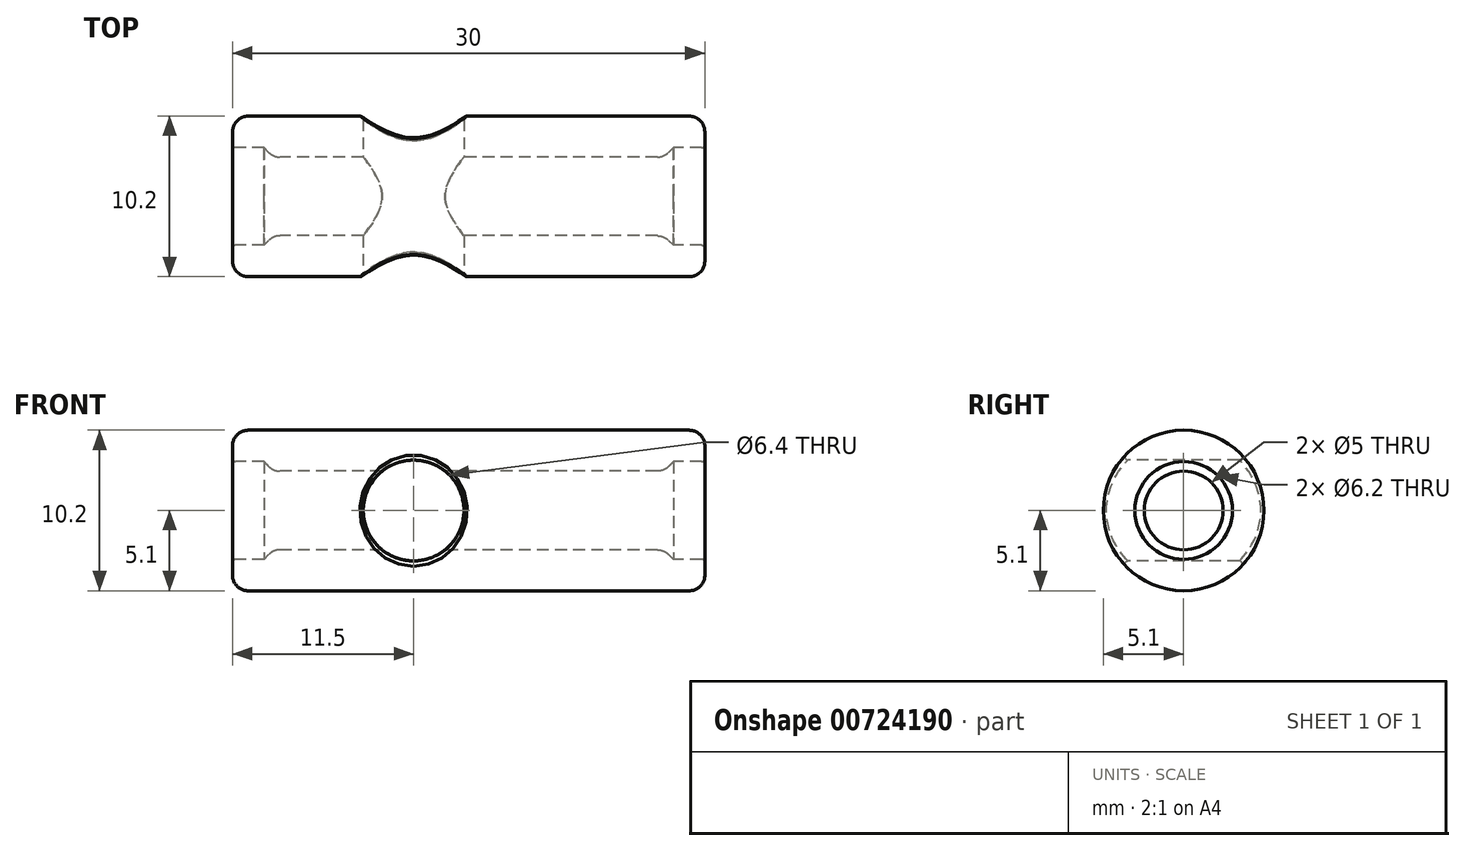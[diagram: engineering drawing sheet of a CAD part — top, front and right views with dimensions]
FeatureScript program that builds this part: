
annotation { "Feature Type Name" : "Feature", "Feature Type Description" : "" }
export const myFeature = defineFeature(function(context is Context, id is Id, definition is map)
    precondition{}
    {
        {
            var Q0;
            Q0=qCreatedBy(makeId("Front.planeOp"),FACE);
            var sketch = newSketch(context, id + "F0", { "sketchPlane" : qUnion([Q0])});
            skLineSegment(sketch, "E0", {"start": v(-15, 3.1) * mm, "end": v(-15, 5.1) * mm});
            skLineSegment(sketch, "E1", {"start": v(-15, 5.1) * mm, "end": v(15, 5.1) * mm});
            skLineSegment(sketch, "E2", {"start": v(15, 5.1) * mm, "end": v(15, 3.1) * mm});
            skLineSegment(sketch, "E3", {"start": v(15, 3.1) * mm, "end": v(13, 3.1) * mm});
            skLineSegment(sketch, "E4", {"start": v(13, 3.1) * mm, "end": v(12.4, 2.5) * mm});
            skLineSegment(sketch, "E5", {"start": v(12.4, 2.5) * mm, "end": v(-12.4, 2.5) * mm});
            skLineSegment(sketch, "E6", {"start": v(-12.4, 2.5) * mm, "end": v(-13, 3.1) * mm});
            skLineSegment(sketch, "E7", {"start": v(-13, 3.1) * mm, "end": v(-15, 3.1) * mm});
            skLineSegment(sketch, "E8", {"start": v(-20, 0) * mm, "end": v(20, 0) * mm, "construction": true});
            skLineSegment(sketch, "E9", {"start": v(0, 0) * mm, "end": v(0, 10.1) * mm, "construction": true});
            skSolve(sketch);
        }
        {
            var Q0;
            Q0 = qSketchRegion(id + "F0", true);
            var Q1;
            Q1=sQuery(id+"F0.wireOp",EDGE,"E8");
            revolve(context, id + "F1", {"surfaceOperationType" : NewSurfaceOperationType.NEW, "entities" : qUnion([Q0]), "axis" : qUnion([Q1]), "revolveType" : RevolveType.FULL});
        }
        {
            var Q0;
            Q0=makeQuery(id+"F1.opRevolve","SWEPT_FACE",FACE,{"disambiguationData":[OSD([sQuery(id+"F0.wireOp",EDGE,"E1")])]});
            var Q1;
            Q1=makeQuery(id+"F1.opRevolve","SWEPT_FACE",FACE,{"disambiguationData":[OSD([sQuery(id+"F0.wireOp",EDGE,"E5")])]});
            fillet(context, id + "F2", {"entities" : qUnion([Q0, Q1]), "radius" : 1 * mm, "tangentPropagation" : true, "allowEdgeOverflow" : false});
        }
        {
            var Q0;
            Q0=qCreatedBy(makeId("Front.planeOp"),FACE);
            var sketch = newSketch(context, id + "F3", { "sketchPlane" : qUnion([Q0])});
            skCircle(sketch, "E10", {"center": v(-3.5, 0) * mm, "radius": 3.2 * mm});
            skSolve(sketch);
        }
        {
            var Q0;
            Q0 = qSketchRegion(id + "F3", true);
            extrude(context, id + "F4", {"entities" : qUnion([Q0]), "operationType" : NewBodyOperationType.REMOVE, "oppositeDirection" : true, "depth" : 25.4 * mm, "offsetDistance" : 25.4 * mm, "hasSecondDirection" : true, "secondDirectionOppositeDirection" : false, "secondDirectionDepth" : 25.4 * mm});
        }
        {
            var Q0;
            Q0=makeQuery(id+"F4.boolean.opBoolean","INTERSECT",EDGE,{"disambiguationData":[OD(1.0)],"derivedFrom":[makeQuery(id+"F1.opRevolve","SWEPT_FACE",FACE,{"disambiguationData":[OSD([sQuery(id+"F0.wireOp",EDGE,"E1")])]}),makeQuery(id+"F4.opExtrude","SWEPT_FACE",FACE,{"disambiguationData":[OSD([sQuery(id+"F3.wireOp",EDGE,"E10")])]})]});
            var Q1;
            Q1=makeQuery(id+"F4.boolean.opBoolean","INTERSECT",EDGE,{"disambiguationData":[OD(0.0)],"derivedFrom":[makeQuery(id+"F1.opRevolve","SWEPT_FACE",FACE,{"disambiguationData":[OSD([sQuery(id+"F0.wireOp",EDGE,"E1")])]}),makeQuery(id+"F4.opExtrude","SWEPT_FACE",FACE,{"disambiguationData":[OSD([sQuery(id+"F3.wireOp",EDGE,"E10")])]})]});
            var Q2;
            Q2=makeQuery(id+"F1.opRevolve","SWEPT_EDGE",EDGE,{"disambiguationData":[OSD([sQuery(id+"F0.wireOp",EDGE,"E2"),sQuery(id+"F0.wireOp",EDGE,"E3")])]});
            var Q3;
            Q3=makeQuery(id+"F1.opRevolve","SWEPT_EDGE",EDGE,{"disambiguationData":[OSD([sQuery(id+"F0.wireOp",EDGE,"E0"),sQuery(id+"F0.wireOp",EDGE,"E7")])]});
            fillet(context, id + "F5", {"entities" : qUnion([Q0, Q1, Q2, Q3]), "radius" : .2 * mm, "tangentPropagation" : true, "allowEdgeOverflow" : false});
        }
    });
